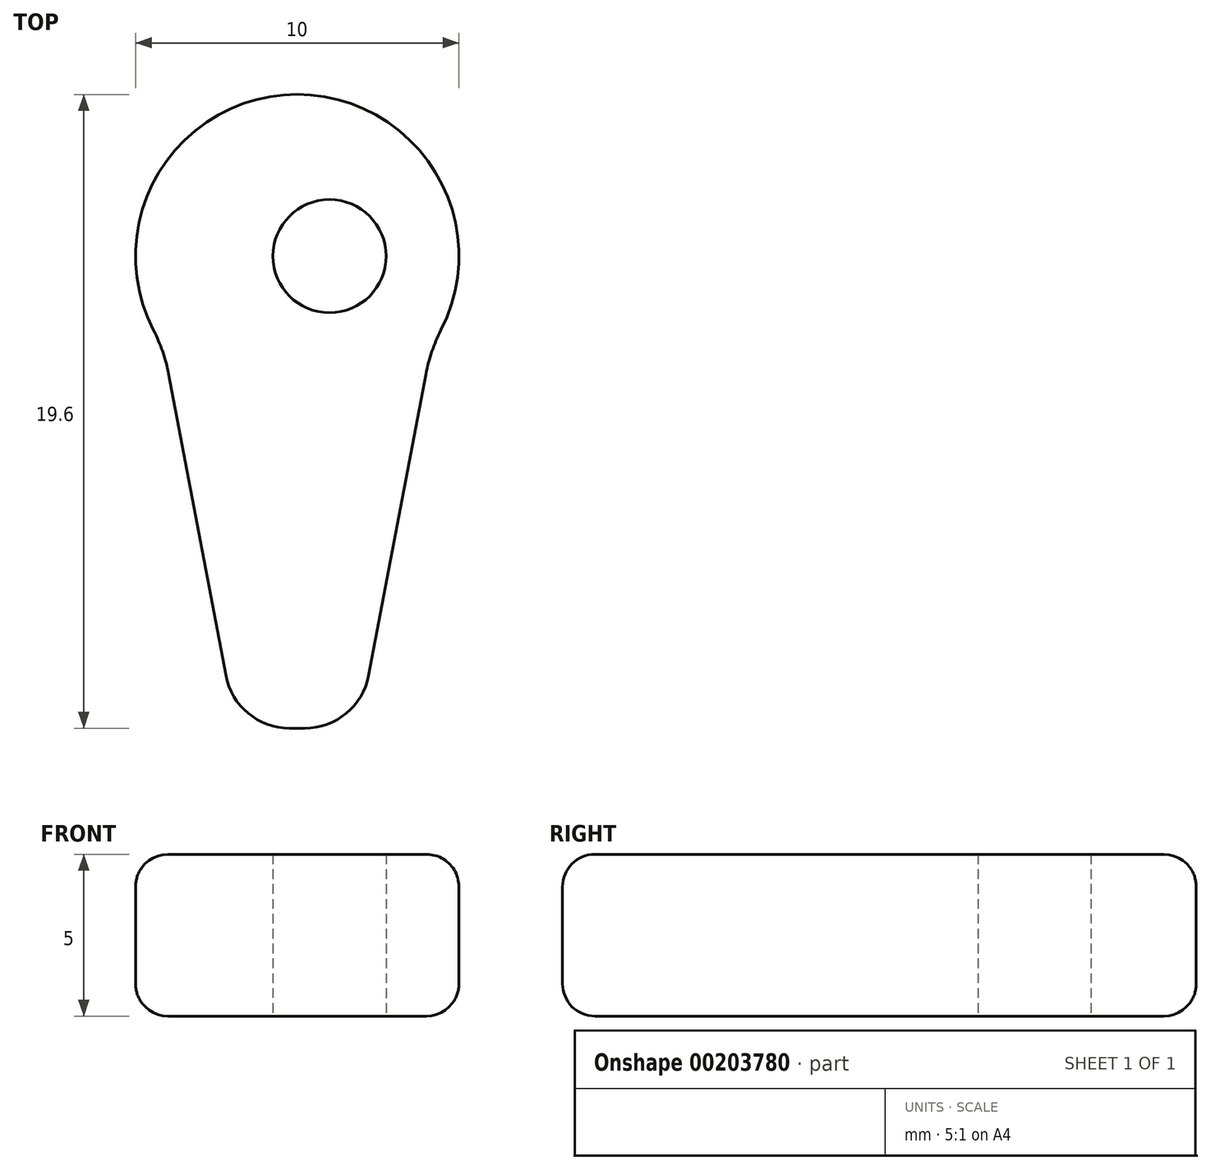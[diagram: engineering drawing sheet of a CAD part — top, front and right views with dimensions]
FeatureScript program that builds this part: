
annotation { "Feature Type Name" : "Feature", "Feature Type Description" : "" }
export const myFeature = defineFeature(function(context is Context, id is Id, definition is map)
    precondition{}
    {
        {
            var Q0;
            Q0=qCreatedBy(makeId("Top.planeOp"),FACE);
            var sketch = newSketch(context, id + "F0", { "sketchPlane" : qUnion([Q0])});
            skArc(sketch, "E0", {"start": v(4.14, -2.8) * mm, "mid": v(0, 5) * mm, "end": v(-4.14, -2.8) * mm});
            skLineSegment(sketch, "E1", {"start": v(0, 0) * mm, "end": v(1, 0) * mm, "construction": true});
            skCircle(sketch, "E2", {"center": v(1, 0) * mm, "radius": 1.75 * mm});
            skLineSegment(sketch, "E3", {"start": v(-4.14, -2.8) * mm, "end": v(-1.9, -14.6) * mm});
            skLineSegment(sketch, "E4.MirrorCS", {"start": v(4.14, -2.8) * mm, "end": v(1.9, -14.6) * mm});
            skLineSegment(sketch, "E5", {"start": v(-1.9, -14.6) * mm, "end": v(1.9, -14.6) * mm});
            skSolve(sketch);
        }
        {
            var Q0;
            Q0=makeQuery(id+"F0.imprint","IMPRINT",FACE,{"disambiguationData":[TD([[makeQuery(id+"F0.imprint","IMPRINT",EDGE,{"derivedFrom":sQuery(id+"F0.wireOp",EDGE,"E0")}),1.0]])]});
            extrude(context, id + "F1", {"entities" : qUnion([Q0]), "depth" : 5 * mm, "symmetric" : true});
        }
        {
            var Q0;
            Q0=makeQuery(id+"F1.opExtrude","SWEPT_EDGE",EDGE,{"disambiguationData":[OSD([sQuery(id+"F0.wireOp",EDGE,"E4.MirrorCS"),sQuery(id+"F0.wireOp",EDGE,"E5")])]});
            var Q1;
            Q1=makeQuery(id+"F1.opExtrude","SWEPT_EDGE",EDGE,{"disambiguationData":[OSD([sQuery(id+"F0.wireOp",EDGE,"E3"),sQuery(id+"F0.wireOp",EDGE,"E5")])]});
            fillet(context, id + "F2", {"entities" : qUnion([Q0, Q1]), "radius" : 2 * mm, "tangentPropagation" : true, "allowEdgeOverflow" : false});
        }
        {
            var Q0;
            Q0=makeQuery(id+"F1.opExtrude","SWEPT_EDGE",EDGE,{"disambiguationData":[OSD([sQuery(id+"F0.wireOp",EDGE,"E0"),sQuery(id+"F0.wireOp",EDGE,"E4.MirrorCS")])]});
            var Q1;
            Q1=makeQuery(id+"F1.opExtrude","SWEPT_EDGE",EDGE,{"disambiguationData":[OSD([sQuery(id+"F0.wireOp",EDGE,"E0"),sQuery(id+"F0.wireOp",EDGE,"E3")])]});
            fillet(context, id + "F3", {"entities" : qUnion([Q0, Q1]), "radius" : 5 * mm, "tangentPropagation" : true, "allowEdgeOverflow" : false});
        }
        {
            var Q0;
            Q0=makeQuery(id+"F1.opExtrude","CAP_EDGE",EDGE,{"disambiguationData":[OSD([sQuery(id+"F0.wireOp",EDGE,"E0")])],"isStart":false});
            var Q1;
            Q1=makeQuery(id+"F1.opExtrude","CAP_EDGE",EDGE,{"disambiguationData":[OSD([sQuery(id+"F0.wireOp",EDGE,"E0")])],"isStart":true});
            fillet(context, id + "F4", {"entities" : qUnion([Q0, Q1]), "radius" : 1 * mm, "tangentPropagation" : true, "allowEdgeOverflow" : false});
        }
    });
